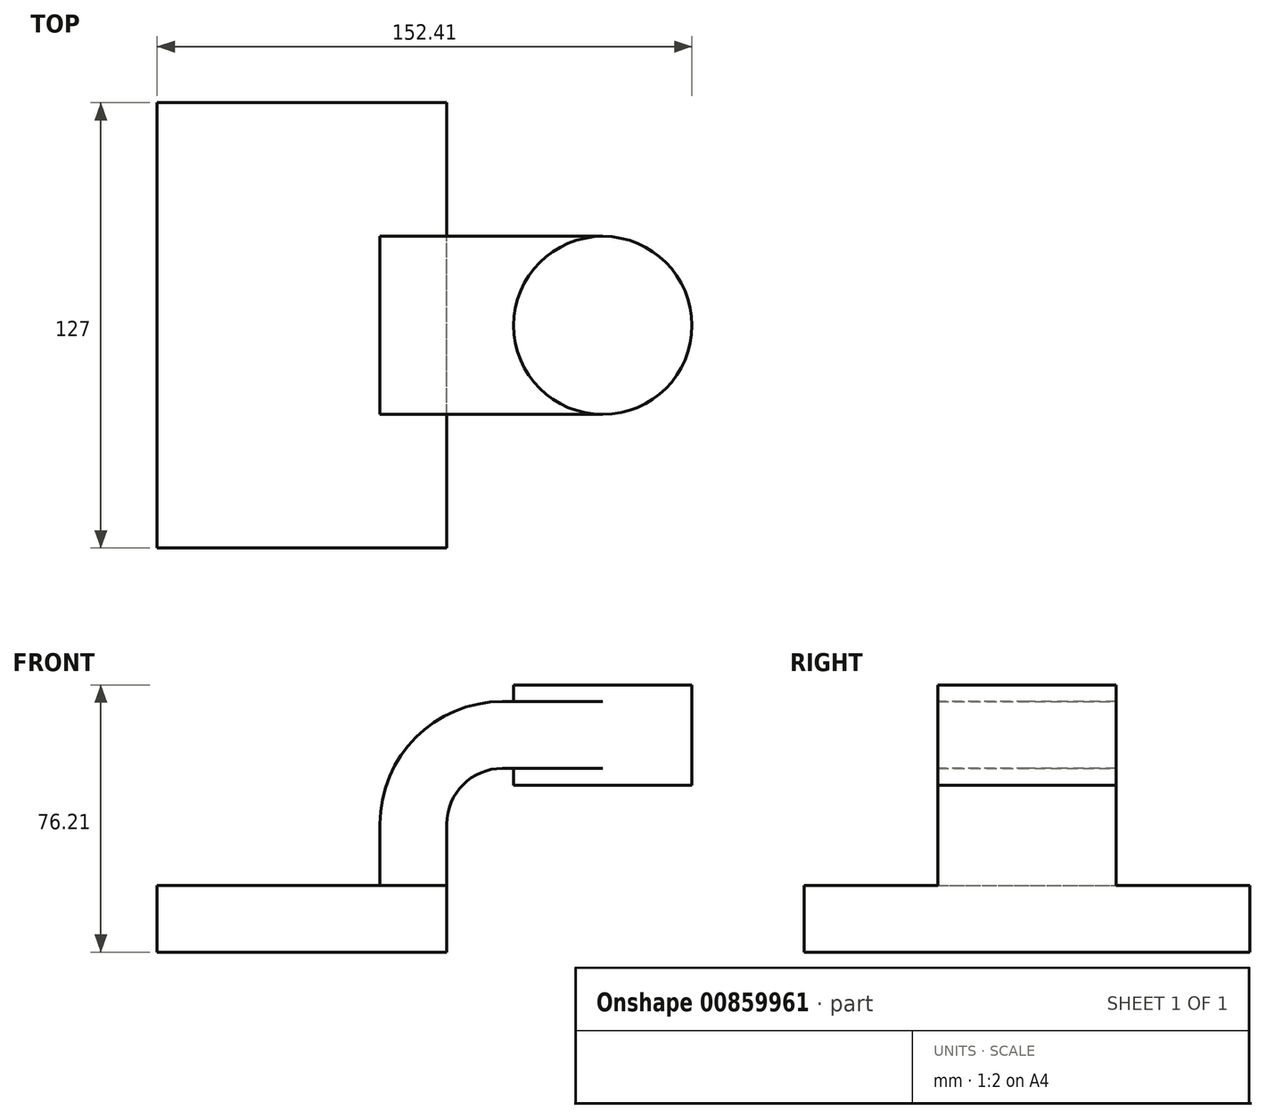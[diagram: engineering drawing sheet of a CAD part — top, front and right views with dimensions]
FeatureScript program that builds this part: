
annotation { "Feature Type Name" : "Feature", "Feature Type Description" : "" }
export const myFeature = defineFeature(function(context is Context, id is Id, definition is map)
    precondition{}
    {
        {
            var Q0;
            Q0=qCreatedBy(makeId("Front.planeOp"),FACE);
            var sketch = newSketch(context, id + "F0", { "sketchPlane" : qUnion([Q0])});
            skLineSegment(sketch, "E0.bottom", {"start": v(-41.28, 9.52) * mm, "end": v(41.27, 9.53) * mm});
            skLineSegment(sketch, "E0.top", {"start": v(-41.28, -9.53) * mm, "end": v(41.28, -9.53) * mm});
            skLineSegment(sketch, "E0.left", {"start": v(-41.28, 9.52) * mm, "end": v(-41.27, -9.53) * mm});
            skLineSegment(sketch, "E0.right", {"start": v(41.28, 9.53) * mm, "end": v(41.28, -9.52) * mm});
            skPoint(sketch, "E0.middle", {"position": v(0, 0) * mm});
            skLineSegment(sketch, "E1.bottom", {"start": v(111.12, 38.1) * mm, "end": v(60.33, 38.1) * mm});
            skLineSegment(sketch, "E1.top", {"start": v(111.12, 66.68) * mm, "end": v(60.33, 66.68) * mm});
            skLineSegment(sketch, "E1.left", {"start": v(111.12, 38.1) * mm, "end": v(111.12, 66.68) * mm});
            skLineSegment(sketch, "E1.right", {"start": v(60.33, 38.1) * mm, "end": v(60.33, 66.68) * mm});
            skPoint(sketch, "E1.middle", {"position": v(85.72, 52.39) * mm});
            skLineSegment(sketch, "E2", {"start": v(41.27, 9.53) * mm, "end": v(41.27, 27) * mm});
            skArc(sketch, "E3", {"start": v(41.27, 27) * mm, "mid": v(45.92, 38.23) * mm, "end": v(57.15, 42.88) * mm});
            skLineSegment(sketch, "E4", {"start": v(57.15, 42.88) * mm, "end": v(85.72, 42.88) * mm});
            skLineSegment(sketch, "E5.0", {"start": v(57.15, 61.93) * mm, "end": v(85.72, 61.93) * mm});
            skArc(sketch, "E5.1", {"start": v(22.23, 27) * mm, "mid": v(32.45, 51.7) * mm, "end": v(57.15, 61.93) * mm});
            skLineSegment(sketch, "E5.2", {"start": v(22.22, 9.53) * mm, "end": v(22.22, 27) * mm});
            skLineSegment(sketch, "E6", {"start": v(85.72, 38.1) * mm, "end": v(85.72, 66.68) * mm});
            skFitSpline(sketch, "E7", {"points": [v(-41.28, 9.52) * mm, v(57.15, 61.93) * mm], "startDerivative": vector(0, 66.9) * mm, "endDerivative": vector(97.38, 0) * mm});
            skSolve(sketch);
        }
        {
            var Q0;
            Q0=makeQuery(id+"F0.imprint","IMPRINT",FACE,{"disambiguationData":[TD([[makeQuery(id+"F0.imprint","IMPRINT",EDGE,{"derivedFrom":sQuery(id+"F0.wireOp",EDGE,"E0.top")}),1.0]])]});
            extrude(context, id + "F1", {"entities" : qUnion([Q0]), "endBound" : BoundingType.SYMMETRIC, "depth" : 127 * mm, "offsetDistance" : 25.4 * mm});
        }
        {
            var Q0;
            {var subQ1=sQuery(id+"F0.wireOp",EDGE,"E2");Q0=makeQuery(id+"F0.imprint","IMPRINT",FACE,{"disambiguationData":[TD([[makeQuery(id+"F0.imprint","IMPRINT",EDGE,{"derivedFrom":subQ1}),1.0]])]});}
            var Q1;
            {var subQ0=sQuery(id+"F0.wireOp",EDGE,"E4");var subQ1=sQuery(id+"F0.wireOp",EDGE,"E1.right");var subQ2=makeQuery(id+"F0.imprint","INTERSECT",VERTEX,{"derivedFrom":[subQ1,subQ0]});Q1=makeQuery(id+"F0.imprint","IMPRINT",FACE,{"disambiguationData":[TD([[makeQuery(id+"F0.imprint","IMPRINT",EDGE,{"disambiguationData":[TD([[subQ2,-1.0]])],"derivedFrom":subQ1}),-1.0]])]});}
            extrude(context, id + "F2", {"entities" : qUnion([Q0, Q1]), "operationType" : NewBodyOperationType.ADD, "endBound" : BoundingType.SYMMETRIC, "depth" : 50.8 * mm, "offsetDistance" : 25.4 * mm});
        }
        {
            var Q0;
            Q0=makeQuery(id+"F0.imprint","IMPRINT",FACE,{"disambiguationData":[TD([[makeQuery(id+"F0.imprint","IMPRINT",EDGE,{"derivedFrom":sQuery(id+"F0.wireOp",EDGE,"E5.1")}),1.0]])]});
            extrude(context, id + "F3", {"entities" : qUnion([Q0]), "operationType" : NewBodyOperationType.ADD, "endBound" : BoundingType.SYMMETRIC, "depth" : 15.88 * mm, "offsetDistance" : 25.4 * mm});
        }
        {
            var Q0;
            {var subQ4=sQuery(id+"F0.wireOp",EDGE,"E1.left");Q0=makeQuery(id+"F0.imprint","IMPRINT",FACE,{"disambiguationData":[TD([[makeQuery(id+"F0.imprint","IMPRINT",EDGE,{"derivedFrom":subQ4}),1.0]])]});}
            var Q1;
            Q1=sQuery(id+"F0.wireOp",EDGE,"E6");
            revolve(context, id + "F4", {"operationType" : NewBodyOperationType.ADD, "surfaceOperationType" : NewSurfaceOperationType.NEW, "entities" : qUnion([Q0]), "axis" : qUnion([Q1]), "revolveType" : RevolveType.FULL});
        }
    });
